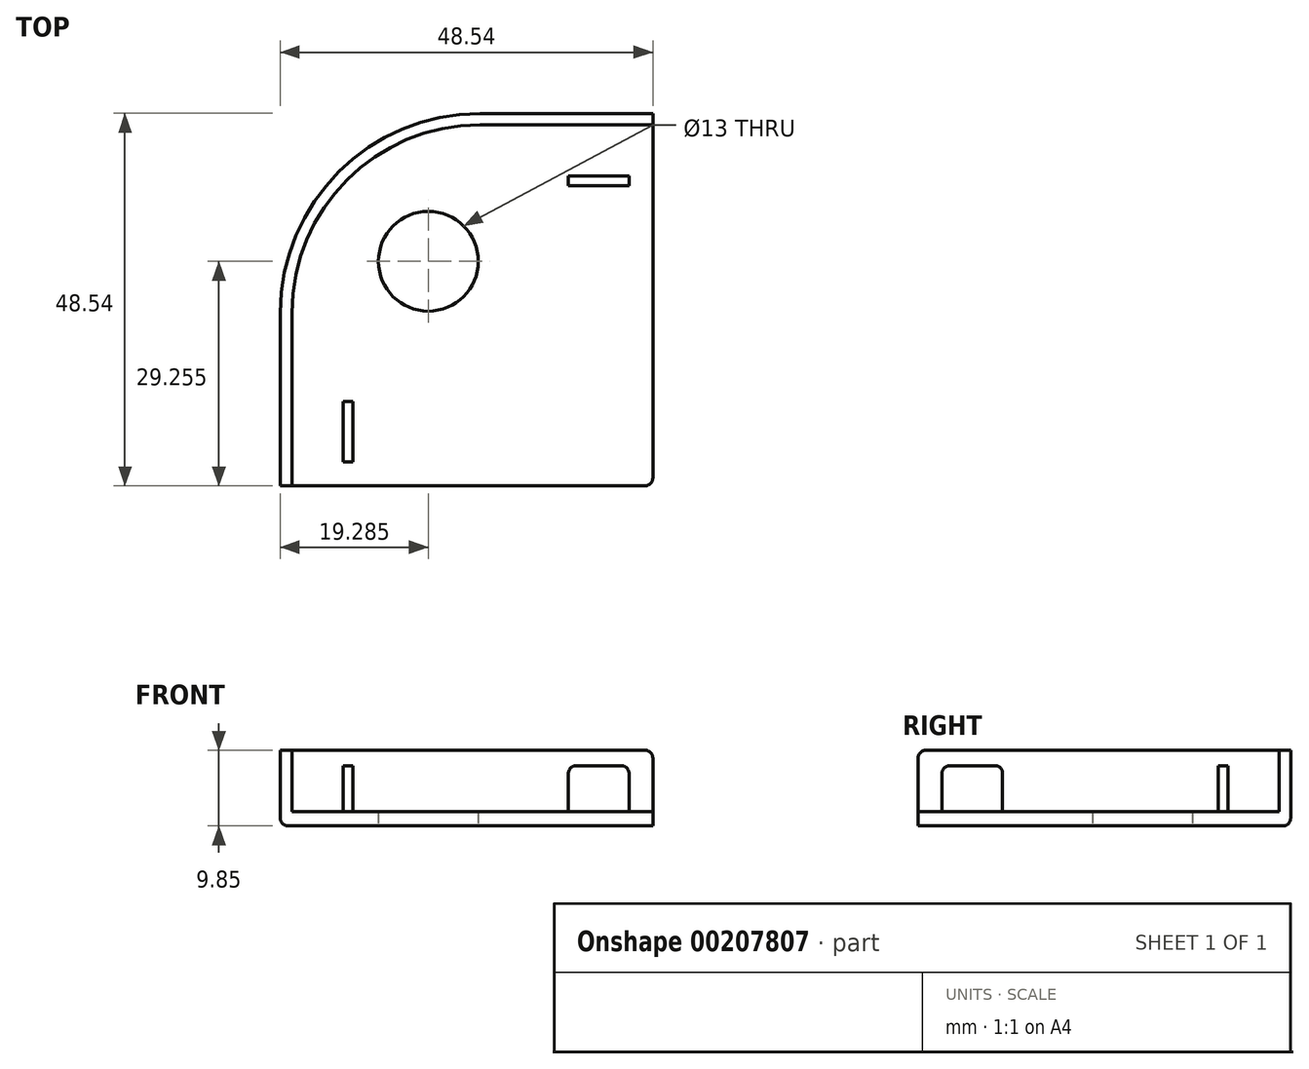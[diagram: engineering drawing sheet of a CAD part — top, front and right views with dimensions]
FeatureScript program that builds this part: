
annotation { "Feature Type Name" : "Feature", "Feature Type Description" : "" }
export const myFeature = defineFeature(function(context is Context, id is Id, definition is map)
    precondition{}
    {
        {
            var Q0;
            Q0=qCreatedBy(makeId("Top.planeOp"),FACE);
            var sketch = newSketch(context, id + "F0", { "sketchPlane" : qUnion([Q0])});
            skLineSegment(sketch, "E0.bottom", {"start": v(24.25, -24.25) * mm, "end": v(-24.29, -24.25) * mm});
            skLineSegment(sketch, "E0.top", {"start": v(24.25, 24.29) * mm, "end": v(1.71, 24.29) * mm});
            skLineSegment(sketch, "E0.left", {"start": v(24.25, -24.25) * mm, "end": v(24.25, 24.29) * mm});
            skLineSegment(sketch, "E0.right", {"start": v(-24.29, -24.25) * mm, "end": v(-24.29, -1.71) * mm});
            skPoint(sketch, "E1.visualSharp", {"position": v(-24.29, 24.29) * mm});
            skArc(sketch, "E1.filletArc", {"start": v(1.71, 24.29) * mm, "mid": v(-16.67, 16.67) * mm, "end": v(-24.29, -1.71) * mm});
            skLineSegment(sketch, "E2", {"start": v(24.25, -24.25) * mm, "end": v(-24.29, 24.29) * mm, "construction": true});
            skCircle(sketch, "E3", {"center": v(-5, 5) * mm, "radius": 6.5 * mm});
            skSolve(sketch);
        }
        {
            var Q0;
            Q0=makeQuery(id+"F0.imprint","IMPRINT",FACE,{"disambiguationData":[TD([[makeQuery(id+"F0.imprint","IMPRINT",EDGE,{"derivedFrom":sQuery(id+"F0.wireOp",EDGE,"E0.bottom")}),-1.0]])]});
            extrude(context, id + "F1", {"entities" : qUnion([Q0]), "flatOperationType" : FlatOperationType.REMOVE, "offsetDistance" : 25 * mm, "depth" : 1.85 * mm, "domain" : OperationDomain.MODEL});
        }
        {
            var Q0;
            Q0=makeQuery(id+"F1.opExtrude","CAP_FACE",FACE,{"disambiguationData":[OSD([sQuery(id+"F0.wireOp",EDGE,"E0.bottom"),sQuery(id+"F0.wireOp",EDGE,"E0.top"),sQuery(id+"F0.wireOp",EDGE,"E0.left"),sQuery(id+"F0.wireOp",EDGE,"E0.right"),sQuery(id+"F0.wireOp",EDGE,"E1.filletArc"),sQuery(id+"F0.wireOp",EDGE,"E3")])],"isStart":false});
            var sketch = newSketch(context, id + "F2", { "sketchPlane" : qUnion([Q0])});
            skLineSegment(sketch, "E4", {"start": v(-24.29, -24.25) * mm, "end": v(-24.29, -1.71) * mm});
            skLineSegment(sketch, "E5", {"start": v(24.25, 24.29) * mm, "end": v(1.71, 24.29) * mm});
            skArc(sketch, "E6", {"start": v(-24.29, -1.71) * mm, "mid": v(-16.67, 16.67) * mm, "end": v(1.71, 24.29) * mm});
            skLineSegment(sketch, "E7", {"start": v(-24.29, -24.25) * mm, "end": v(-22.79, -24.25) * mm});
            skLineSegment(sketch, "E8", {"start": v(-22.79, -24.25) * mm, "end": v(-22.79, -1.71) * mm});
            skLineSegment(sketch, "E9", {"start": v(24.25, 24.29) * mm, "end": v(24.25, 22.79) * mm});
            skLineSegment(sketch, "E10", {"start": v(24.25, 22.79) * mm, "end": v(1.71, 22.79) * mm});
            skArc(sketch, "E11", {"start": v(-22.79, -1.71) * mm, "mid": v(-15.61, 15.61) * mm, "end": v(1.71, 22.79) * mm});
            skSolve(sketch);
        }
        {
            var Q0;
            Q0=makeQuery(id+"F2.imprint","IMPRINT",FACE,{"disambiguationData":[TD([[makeQuery(id+"F2.imprint","IMPRINT",EDGE,{"derivedFrom":sQuery(id+"F2.wireOp",EDGE,"E4")}),-1.0]])]});
            extrude(context, id + "F3", {"entities" : qUnion([Q0]), "operationType" : NewBodyOperationType.ADD, "flatOperationType" : FlatOperationType.REMOVE, "offsetDistance" : 25 * mm, "depth" : 8 * mm, "domain" : OperationDomain.MODEL});
        }
        {
            var Q0;
            Q0=makeQuery(id+"F1.opExtrude","CAP_FACE",FACE,{"disambiguationData":[OSD([sQuery(id+"F0.wireOp",EDGE,"E0.bottom"),sQuery(id+"F0.wireOp",EDGE,"E0.top"),sQuery(id+"F0.wireOp",EDGE,"E0.left"),sQuery(id+"F0.wireOp",EDGE,"E0.right"),sQuery(id+"F0.wireOp",EDGE,"E1.filletArc"),sQuery(id+"F0.wireOp",EDGE,"E3")])],"isStart":false});
            var sketch = newSketch(context, id + "F4", { "sketchPlane" : qUnion([Q0])});
            skLineSegment(sketch, "E12.bottom", {"start": v(-16.14, -13.25) * mm, "end": v(-14.84, -13.25) * mm});
            skLineSegment(sketch, "E12.top", {"start": v(-16.14, -21.14) * mm, "end": v(-14.84, -21.14) * mm});
            skLineSegment(sketch, "E12.left", {"start": v(-16.14, -13.25) * mm, "end": v(-16.14, -21.14) * mm});
            skLineSegment(sketch, "E12.right", {"start": v(-14.84, -13.25) * mm, "end": v(-14.84, -21.14) * mm});
            skLineSegment(sketch, "E13.bottom", {"start": v(13.25, 16.14) * mm, "end": v(21.14, 16.14) * mm});
            skLineSegment(sketch, "E13.top", {"start": v(13.25, 14.84) * mm, "end": v(21.14, 14.84) * mm});
            skLineSegment(sketch, "E13.left", {"start": v(13.25, 16.14) * mm, "end": v(13.25, 14.84) * mm});
            skLineSegment(sketch, "E13.right", {"start": v(21.14, 16.14) * mm, "end": v(21.14, 14.84) * mm});
            skSolve(sketch);
        }
        {
            var Q0;
            Q0 = qSketchRegion(id + "F4", true);
            extrude(context, id + "F5", {"entities" : qUnion([Q0]), "operationType" : NewBodyOperationType.ADD, "flatOperationType" : FlatOperationType.REMOVE, "offsetDistance" : 25 * mm, "depth" : 6 * mm, "domain" : OperationDomain.MODEL});
        }
        {
            var Q0;
            Q0=makeQuery(id+"F3.opExtrude","CAP_EDGE",EDGE,{"disambiguationData":[OSD([sQuery(id+"F2.wireOp",EDGE,"E7")])],"isStart":false});
            var Q1;
            Q1=makeQuery(id+"F3.opExtrude","CAP_EDGE",EDGE,{"disambiguationData":[OSD([sQuery(id+"F2.wireOp",EDGE,"E9")])],"isStart":false});
            var Q2;
            Q2=makeQuery(id+"F1.opExtrude","CAP_EDGE",EDGE,{"disambiguationData":[OSD([sQuery(id+"F0.wireOp",EDGE,"E0.right")])],"isStart":true});
            var Q3;
            Q3=makeQuery(id+"F5.opExtrude","CAP_EDGE",EDGE,{"disambiguationData":[OSD([sQuery(id+"F4.wireOp",EDGE,"E12.top")])],"isStart":false});
            var Q4;
            Q4=makeQuery(id+"F5.opExtrude","CAP_EDGE",EDGE,{"disambiguationData":[OSD([sQuery(id+"F4.wireOp",EDGE,"E12.bottom")])],"isStart":false});
            var Q5;
            Q5=makeQuery(id+"F5.opExtrude","CAP_EDGE",EDGE,{"disambiguationData":[OSD([sQuery(id+"F4.wireOp",EDGE,"E13.left")])],"isStart":false});
            var Q6;
            Q6=makeQuery(id+"F5.opExtrude","CAP_EDGE",EDGE,{"disambiguationData":[OSD([sQuery(id+"F4.wireOp",EDGE,"E13.right")])],"isStart":false});
            var Q7;
            Q7=makeQuery(id+"F1.opExtrude","SWEPT_EDGE",EDGE,{"disambiguationData":[OSD([sQuery(id+"F0.wireOp",EDGE,"E0.bottom"),sQuery(id+"F0.wireOp",EDGE,"E0.left")])]});
            fillet(context, id + "F6", {"entities" : qUnion([Q0, Q1, Q2, Q3, Q4, Q5, Q6, Q7]), "radius" : 1 * mm, "tangentPropagation" : true, "allowEdgeOverflow" : false});
        }
    });
